# Revit family: Gira_260567
name_source: partatom
category: Electrical Fixtures
revit_build: Autodesk Revit 2017 (Build: 20160225_1515(x64)
units: mm (PartAtom-declared; Revit-internal decimal feet)

## family parameters
Cut with Voids When Loaded = No
Host = Face
Maintain Annotation Orientation = Yes
Part Type = Normal
Room Calculation Point = No
Round Connector Dimension = Use Diameter
Shared = No

## types (1)
- Gira Keyless In Codetastatur Gira TX_44 (WG UP) Anthrazit
    Andere Bussysteme = sonstige
    Ausführung = Codeschloss
    Ausführung der Oberfläche = nicht zutreffend
    Available = Yes
    Bussystem Funkbus = No
    Bussystem KNX = No
    Bussystem KNX-Funk = No
    Bussystem LON = No
    Bussystem Powernet = No
    Category = Bussystem-Zutrittskontrolleinrichtung
    Data sheet (1) = https://katalog.gira.de
    Default Elevation = 1219 mm
    Farbe = anthrazit
    GTIN = 4010337051435
    HAN = 260567
    HeinzeBIM = https://bimportal.heinze.de
    Keynote = TX44_Komplettgerät_Schalten und Tasten
    Manufacturer URL = https://www.gira.de
    Mit Busankopplung = Yes
    Montageart = unter Putz
    Name = Gira Keyless In Codetastatur Gira TX_44 (WG UP) Anthrazit
    Oberfläche = sonstige
    Region = DE
    Schutzart (IP) = IP44
    Transparent = No
    URL = http://katalog.gira.de
    Werkstoff = sonstige
    Werkstoffgüte = sonstige

## geometry (parser evidence)
native form markers: Blend x2, Sweep x3
no freeform markers — native parametric forms only
